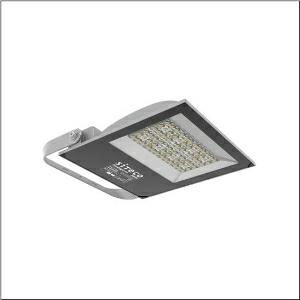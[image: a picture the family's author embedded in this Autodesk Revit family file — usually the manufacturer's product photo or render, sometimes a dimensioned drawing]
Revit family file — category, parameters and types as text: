
# Revit family: floodlight_fl_41_midi___pl32_5xa8581b2121_e0cb
name_source: partatom
category: Lighting Fixtures
units: mm (PartAtom-declared; Revit-internal decimal feet)

## family parameters
Cut with Voids When Loaded = No
Host = Face
Light Source = No
Part Type = Normal
Room Calculation Point = No
Round Connector Dimension = Use Diameter
Shared = No

## types (1)
- --- (1 x LED, 26000 lm, 200 W, 4000K)
    Apparent Load = 200 VA
    CIE Flux Codes = 38 75 98 100 100
    Color Rendering = 70
    Color Temperature = 4000K
    Default Elevation = 1800 mm
    Description = Floodlight FL 41 midi, floodlight, primary light control with lens, of PMMA, primary optical cover: protective disc, transparent, light distribution: PL32, light emission: direct distribution, installation type: surface-mounted, LED, High Power LED, rated luminous flux: 26.000lm, luminous efficacy: 130lm/W, light colour: 740, colour temperature: 4000K, control gear: ON/OFF Multilumen, with cable, 3x 1.5mm², mains connection: 220..240V, AC, 50/60Hz, connection cable pre-assembled, cable length: 2m, rated input power: 200W, luminaire housing, of diecast aluminium, powder-coated, metallic grey (RAL 9006), length: 375mm, width: 335mm, height: 65mm, protection rating (complete): IP65, insulation class (complete): insulation class I (protective earthing), certification: CE, ENEC, impact resistance: IK08, permissible operating ambient temperature: -40..+40°C, permissible storage temperature: -40..+60°C, packaging unit: 1 piece

Light Distribution: PL32
    Height = 66 mm
    Lamp = 1 x LED
    Lamp Light Flux = 26000 lm
    Lamp Power = 200 W
    Lamp count = 1
    Length = 323 mm
    Luminous efficacy = 130 lm/W
    Manufacturer = Siteco
    ModVariant = No
    Model = 5XA8581B2121
    Mounting Place = Ceiling
    Mounting Type = Surface mounted
    Number of Poles = 1
    OnlyDefault = Yes
    Power Factor = 1
    Product Name = Floodlight FL 41 midi | PL32
    Product group = floodlight | ceiling mounted
    ProductGroupID = 305
    Protection Class = Protection class I
    Protection Degree = IP 65
    RLX_Detail_Level = 1
    RLX_Emergency_Light_Flux = 0 lm
    RLX_Emergency_Type = 0
    RLX_Emergency_Type_DB = No
    RlxData = <blob elided: 27413 chars, md5=d1611535>
    Socket = socket
    Standby Power = 0 W
    System Light Flux = 26000 lm
    System Power = 200 W
    Type Comments = factory setting: luminous flux: 100 % | (OFF | OFF | OFF)
    Type Image = l_1248229.jpg
    URL = http://relux.com
    VarID = @adj_131193
    Voltage = 0 V
    Weight = 0.00 kg
    Width = 331 mm

## geometry (parser evidence)
native form markers: Blend x4, Sweep x12
no freeform markers — native parametric forms only
